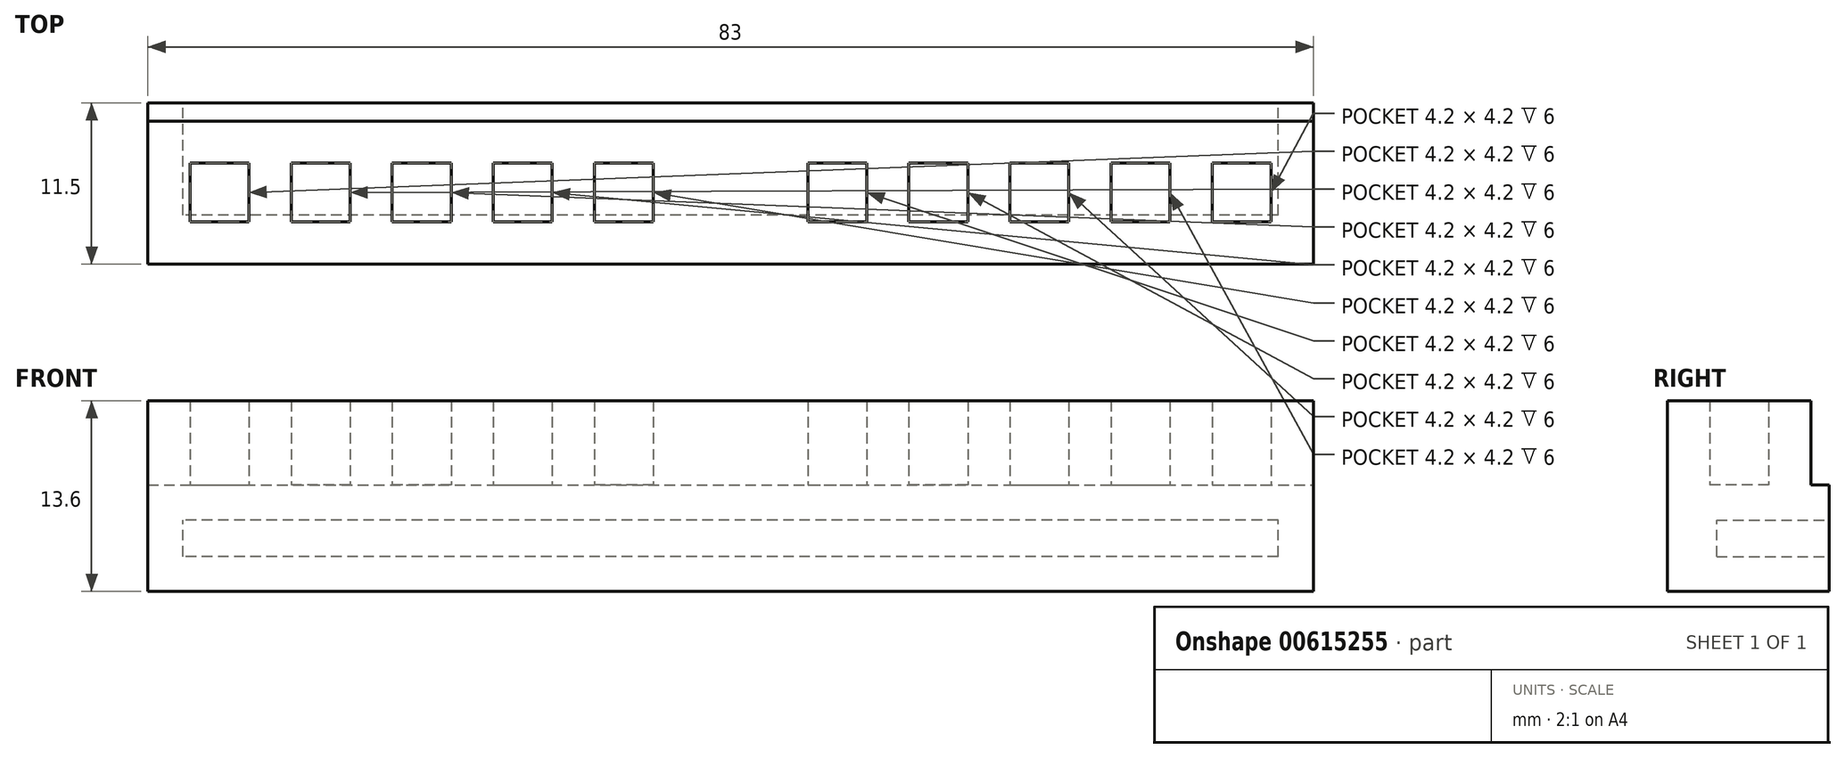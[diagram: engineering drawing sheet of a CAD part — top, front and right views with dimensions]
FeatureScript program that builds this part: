
annotation { "Feature Type Name" : "Feature", "Feature Type Description" : "" }
export const myFeature = defineFeature(function(context is Context, id is Id, definition is map)
    precondition{}
    {
        {
            var Q0;
            Q0=qCreatedBy(makeId("Front.planeOp"),FACE);
            var sketch = newSketch(context, id + "F0", { "sketchPlane" : qUnion([Q0])});
            skLineSegment(sketch, "E0.bottom", {"start": v(41.5, -3.8) * mm, "end": v(-41.5, -3.8) * mm});
            skLineSegment(sketch, "E0.top", {"start": v(41.5, 3.8) * mm, "end": v(-41.5, 3.8) * mm});
            skLineSegment(sketch, "E0.left", {"start": v(41.5, -3.8) * mm, "end": v(41.5, 3.8) * mm});
            skLineSegment(sketch, "E0.right", {"start": v(-41.5, -3.8) * mm, "end": v(-41.5, 3.8) * mm});
            skPoint(sketch, "E0.middle", {"position": v(0, 0) * mm});
            skLineSegment(sketch, "E1.bottom", {"start": v(39, -1.3) * mm, "end": v(-39, -1.3) * mm});
            skLineSegment(sketch, "E1.top", {"start": v(39, 1.3) * mm, "end": v(-39, 1.3) * mm});
            skLineSegment(sketch, "E1.left", {"start": v(39, -1.3) * mm, "end": v(39, 1.3) * mm});
            skLineSegment(sketch, "E1.right", {"start": v(-39, -1.3) * mm, "end": v(-39, 1.3) * mm});
            skSolve(sketch);
        }
        {
            var Q0;
            Q0=makeQuery(id+"F0.imprint","IMPRINT",FACE,{"disambiguationData":[TD([[makeQuery(id+"F0.imprint","IMPRINT",EDGE,{"derivedFrom":sQuery(id+"F0.wireOp",EDGE,"E0.bottom")}),-1.0]])]});
            extrude(context, id + "F1", {"entities" : qUnion([Q0]), "depth" : 8 * mm, "offsetDistance" : 25 * mm});
        }
        {
            var Q0;
            Q0=makeQuery(id+"F1.opExtrude","CAP_FACE",FACE,{"disambiguationData":[OSD([sQuery(id+"F0.wireOp",EDGE,"E0.bottom"),sQuery(id+"F0.wireOp",EDGE,"E0.top"),sQuery(id+"F0.wireOp",EDGE,"E0.left"),sQuery(id+"F0.wireOp",EDGE,"E0.right"),sQuery(id+"F0.wireOp",EDGE,"E1.bottom"),sQuery(id+"F0.wireOp",EDGE,"E1.top"),sQuery(id+"F0.wireOp",EDGE,"E1.left"),sQuery(id+"F0.wireOp",EDGE,"E1.right")])],"isStart":false});
            var sketch = newSketch(context, id + "F2", { "sketchPlane" : qUnion([Q0])});
            skLineSegment(sketch, "E2.bottom", {"start": v(-41.5, 3.8) * mm, "end": v(41.5, 3.8) * mm});
            skLineSegment(sketch, "E2.top", {"start": v(-41.5, -3.8) * mm, "end": v(41.5, -3.8) * mm});
            skLineSegment(sketch, "E2.left", {"start": v(-41.5, 3.8) * mm, "end": v(-41.5, -3.8) * mm});
            skLineSegment(sketch, "E2.right", {"start": v(41.5, 3.8) * mm, "end": v(41.5, -3.8) * mm});
            skSolve(sketch);
        }
        {
            var Q0;
            Q0=makeQuery(id+"F2.imprint","IMPRINT",FACE,{"disambiguationData":[TD([[makeQuery(id+"F2.imprint","IMPRINT",EDGE,{"derivedFrom":sQuery(id+"F2.wireOp",EDGE,"E2.bottom")}),1.0]])]});
            var Q1;
            Q1=makeQuery(id+"F2.imprint","IMPRINT",FACE,{"disambiguationData":[TD([[makeQuery(id+"F2.imprint","IMPRINT",EDGE,{"derivedFrom":makeQuery(id+"F1.opExtrude","CAP_EDGE",EDGE,{"disambiguationData":[OSD([sQuery(id+"F0.wireOp",EDGE,"E1.bottom")])],"isStart":false})}),-1.0]])]});
            extrude(context, id + "F3", {"entities" : qUnion([Q0, Q1]), "operationType" : NewBodyOperationType.ADD, "depth" : 3.5 * mm, "offsetDistance" : 25 * mm});
        }
        {
            var Q0;
            Q0=makeQuery(id+"F3.boolean.opBoolean","MERGE",FACE,{"derivedFrom":[makeQuery(id+"F1.opExtrude","SWEPT_FACE",FACE,{"disambiguationData":[OSD([sQuery(id+"F0.wireOp",EDGE,"E0.top")])]}),makeQuery(id+"F3.opExtrude","SWEPT_FACE",FACE,{"disambiguationData":[OSD([sQuery(id+"F2.wireOp",EDGE,"E2.bottom")])]})]});
            var sketch = newSketch(context, id + "F4", { "sketchPlane" : qUnion([Q0])});
            skLineSegment(sketch, "E3.bottom", {"start": v(-41.5, -11.5) * mm, "end": v(41.5, -11.5) * mm});
            skLineSegment(sketch, "E3.top", {"start": v(-41.5, -1.3) * mm, "end": v(41.5, -1.3) * mm});
            skLineSegment(sketch, "E3.left", {"start": v(-41.5, -11.5) * mm, "end": v(-41.5, -1.3) * mm});
            skLineSegment(sketch, "E3.right", {"start": v(41.5, -11.5) * mm, "end": v(41.5, -1.3) * mm});
            skLineSegment(sketch, "E4", {"start": v(-5.5, -1.3) * mm, "end": v(-5.5, -11.5) * mm});
            skLineSegment(sketch, "E5", {"start": v(-9.7, -1.3) * mm, "end": v(-9.7, -11.5) * mm});
            skLineSegment(sketch, "E6", {"start": v(-12.7, -1.3) * mm, "end": v(-12.7, -11.5) * mm});
            skLineSegment(sketch, "E7", {"start": v(-16.9, -1.3) * mm, "end": v(-16.9, -11.5) * mm});
            skLineSegment(sketch, "E8", {"start": v(-19.9, -1.3) * mm, "end": v(-19.9, -11.5) * mm});
            skLineSegment(sketch, "E9", {"start": v(-24.1, -1.3) * mm, "end": v(-24.1, -11.5) * mm});
            skLineSegment(sketch, "E10", {"start": v(-27.1, -1.3) * mm, "end": v(-27.1, -11.5) * mm});
            skLineSegment(sketch, "E11", {"start": v(-31.3, -1.3) * mm, "end": v(-31.3, -11.5) * mm});
            skLineSegment(sketch, "E12", {"start": v(-34.3, -1.3) * mm, "end": v(-34.3, -11.5) * mm});
            skLineSegment(sketch, "E13", {"start": v(-38.5, -1.3) * mm, "end": v(-38.5, -11.5) * mm});
            skLineSegment(sketch, "E14", {"start": v(0, 0) * mm, "end": v(0, -13.13) * mm, "construction": true});
            skLineSegment(sketch, "E15.MirrorCS", {"start": v(38.5, -1.3) * mm, "end": v(38.5, -11.5) * mm});
            skLineSegment(sketch, "E16.MirrorCS", {"start": v(19.9, -1.3) * mm, "end": v(19.9, -11.5) * mm});
            skLineSegment(sketch, "E17.MirrorCS", {"start": v(24.1, -1.3) * mm, "end": v(24.1, -11.5) * mm});
            skLineSegment(sketch, "E18.MirrorCS", {"start": v(34.3, -1.3) * mm, "end": v(34.3, -11.5) * mm});
            skLineSegment(sketch, "E19.MirrorCS", {"start": v(27.1, -1.3) * mm, "end": v(27.1, -11.5) * mm});
            skLineSegment(sketch, "E20.MirrorCS", {"start": v(16.9, -1.3) * mm, "end": v(16.9, -11.5) * mm});
            skLineSegment(sketch, "E21.MirrorCS", {"start": v(9.7, -1.3) * mm, "end": v(9.7, -11.5) * mm});
            skLineSegment(sketch, "E22.MirrorCS", {"start": v(12.7, -1.3) * mm, "end": v(12.7, -11.5) * mm});
            skLineSegment(sketch, "E23.MirrorCS", {"start": v(31.3, -1.3) * mm, "end": v(31.3, -11.5) * mm});
            skLineSegment(sketch, "E24.MirrorCS", {"start": v(5.5, -1.3) * mm, "end": v(5.5, -11.5) * mm});
            skLineSegment(sketch, "E25", {"start": v(-41.5, -4.3) * mm, "end": v(41.5, -4.3) * mm});
            skLineSegment(sketch, "E26", {"start": v(41.5, -8.5) * mm, "end": v(-41.5, -8.5) * mm});
            skSolve(sketch);
        }
        {
            var Q0;
            {var subQ1=sQuery(id+"F4.wireOp",EDGE,"E3.top");var subQ3=sQuery(id+"F4.wireOp",EDGE,"E13");var subQ4=makeQuery(id+"F4.imprint","INTERSECT",VERTEX,{"derivedFrom":[subQ1,subQ3]});Q0=makeQuery(id+"F4.imprint","IMPRINT",FACE,{"disambiguationData":[TD([[makeQuery(id+"F4.imprint","IMPRINT",EDGE,{"disambiguationData":[TD([[subQ4,-1.0]])],"derivedFrom":subQ3}),-1.0]])]});}
            var Q1;
            {var subQ0=sQuery(id+"F4.wireOp",EDGE,"E25");var subQ1=sQuery(id+"F4.wireOp",EDGE,"E3.left");var subQ2=makeQuery(id+"F4.imprint","INTERSECT",VERTEX,{"derivedFrom":[subQ1,subQ0]});Q1=makeQuery(id+"F4.imprint","IMPRINT",FACE,{"disambiguationData":[TD([[makeQuery(id+"F4.imprint","IMPRINT",EDGE,{"disambiguationData":[TD([[subQ2,1.0]])],"derivedFrom":subQ1}),-1.0]])]});}
            var Q2;
            {var subQ0=sQuery(id+"F4.wireOp",EDGE,"E12");var subQ1=sQuery(id+"F4.wireOp",EDGE,"E3.top");var subQ2=makeQuery(id+"F4.imprint","INTERSECT",VERTEX,{"derivedFrom":[subQ1,subQ0]});Q2=makeQuery(id+"F4.imprint","IMPRINT",FACE,{"disambiguationData":[TD([[makeQuery(id+"F4.imprint","IMPRINT",EDGE,{"disambiguationData":[TD([[subQ2,1.0]])],"derivedFrom":subQ1}),-1.0]])]});}
            var Q3;
            {var subQ0=sQuery(id+"F4.wireOp",EDGE,"E3.left");var subQ1=sQuery(id+"F4.wireOp",EDGE,"E3.bottom");var subQ2=makeQuery(id+"F4.imprint","INTERSECT",VERTEX,{"derivedFrom":[subQ1,subQ0]});Q3=makeQuery(id+"F4.imprint","IMPRINT",FACE,{"disambiguationData":[TD([[makeQuery(id+"F4.imprint","IMPRINT",EDGE,{"disambiguationData":[TD([[subQ2,1.0]])],"derivedFrom":subQ1}),-1.0]])]});}
            var Q4;
            {var subQ0=sQuery(id+"F4.wireOp",EDGE,"E12");var subQ1=sQuery(id+"F4.wireOp",EDGE,"E3.bottom");var subQ2=makeQuery(id+"F4.imprint","INTERSECT",VERTEX,{"derivedFrom":[subQ1,subQ0]});Q4=makeQuery(id+"F4.imprint","IMPRINT",FACE,{"disambiguationData":[TD([[makeQuery(id+"F4.imprint","IMPRINT",EDGE,{"disambiguationData":[TD([[subQ2,-1.0]])],"derivedFrom":subQ1}),-1.0]])]});}
            var Q5;
            {var subQ0=sQuery(id+"F4.wireOp",EDGE,"E11");var subQ1=sQuery(id+"F4.wireOp",EDGE,"E3.bottom");var subQ2=makeQuery(id+"F4.imprint","INTERSECT",VERTEX,{"derivedFrom":[subQ1,subQ0]});Q5=makeQuery(id+"F4.imprint","IMPRINT",FACE,{"disambiguationData":[TD([[makeQuery(id+"F4.imprint","IMPRINT",EDGE,{"disambiguationData":[TD([[subQ2,-1.0]])],"derivedFrom":subQ1}),-1.0]])]});}
            var Q6;
            {var subQ0=sQuery(id+"F4.wireOp",EDGE,"E25");var subQ1=sQuery(id+"F4.wireOp",EDGE,"E11");var subQ2=makeQuery(id+"F4.imprint","INTERSECT",VERTEX,{"derivedFrom":[subQ1,subQ0]});Q6=makeQuery(id+"F4.imprint","IMPRINT",FACE,{"disambiguationData":[TD([[makeQuery(id+"F4.imprint","IMPRINT",EDGE,{"disambiguationData":[TD([[subQ2,-1.0]])],"derivedFrom":subQ1}),-1.0]])]});}
            var Q7;
            {var subQ0=sQuery(id+"F4.wireOp",EDGE,"E11");var subQ1=sQuery(id+"F4.wireOp",EDGE,"E3.top");var subQ2=makeQuery(id+"F4.imprint","INTERSECT",VERTEX,{"derivedFrom":[subQ1,subQ0]});Q7=makeQuery(id+"F4.imprint","IMPRINT",FACE,{"disambiguationData":[TD([[makeQuery(id+"F4.imprint","IMPRINT",EDGE,{"disambiguationData":[TD([[subQ2,1.0]])],"derivedFrom":subQ1}),-1.0]])]});}
            var Q8;
            {var subQ0=sQuery(id+"F4.wireOp",EDGE,"E10");var subQ1=sQuery(id+"F4.wireOp",EDGE,"E3.top");var subQ2=makeQuery(id+"F4.imprint","INTERSECT",VERTEX,{"derivedFrom":[subQ1,subQ0]});Q8=makeQuery(id+"F4.imprint","IMPRINT",FACE,{"disambiguationData":[TD([[makeQuery(id+"F4.imprint","IMPRINT",EDGE,{"disambiguationData":[TD([[subQ2,1.0]])],"derivedFrom":subQ1}),-1.0]])]});}
            var Q9;
            {var subQ0=sQuery(id+"F4.wireOp",EDGE,"E10");var subQ1=sQuery(id+"F4.wireOp",EDGE,"E3.bottom");var subQ2=makeQuery(id+"F4.imprint","INTERSECT",VERTEX,{"derivedFrom":[subQ1,subQ0]});Q9=makeQuery(id+"F4.imprint","IMPRINT",FACE,{"disambiguationData":[TD([[makeQuery(id+"F4.imprint","IMPRINT",EDGE,{"disambiguationData":[TD([[subQ2,-1.0]])],"derivedFrom":subQ1}),-1.0]])]});}
            var Q10;
            {var subQ0=sQuery(id+"F4.wireOp",EDGE,"E9");var subQ1=sQuery(id+"F4.wireOp",EDGE,"E3.bottom");var subQ2=makeQuery(id+"F4.imprint","INTERSECT",VERTEX,{"derivedFrom":[subQ1,subQ0]});Q10=makeQuery(id+"F4.imprint","IMPRINT",FACE,{"disambiguationData":[TD([[makeQuery(id+"F4.imprint","IMPRINT",EDGE,{"disambiguationData":[TD([[subQ2,-1.0]])],"derivedFrom":subQ1}),-1.0]])]});}
            var Q11;
            {var subQ0=sQuery(id+"F4.wireOp",EDGE,"E8");var subQ1=sQuery(id+"F4.wireOp",EDGE,"E3.bottom");var subQ2=makeQuery(id+"F4.imprint","INTERSECT",VERTEX,{"derivedFrom":[subQ1,subQ0]});Q11=makeQuery(id+"F4.imprint","IMPRINT",FACE,{"disambiguationData":[TD([[makeQuery(id+"F4.imprint","IMPRINT",EDGE,{"disambiguationData":[TD([[subQ2,-1.0]])],"derivedFrom":subQ1}),-1.0]])]});}
            var Q12;
            {var subQ0=sQuery(id+"F4.wireOp",EDGE,"E8");var subQ1=sQuery(id+"F4.wireOp",EDGE,"E3.top");var subQ2=makeQuery(id+"F4.imprint","INTERSECT",VERTEX,{"derivedFrom":[subQ1,subQ0]});Q12=makeQuery(id+"F4.imprint","IMPRINT",FACE,{"disambiguationData":[TD([[makeQuery(id+"F4.imprint","IMPRINT",EDGE,{"disambiguationData":[TD([[subQ2,1.0]])],"derivedFrom":subQ1}),-1.0]])]});}
            var Q13;
            {var subQ0=sQuery(id+"F4.wireOp",EDGE,"E9");var subQ1=sQuery(id+"F4.wireOp",EDGE,"E3.top");var subQ2=makeQuery(id+"F4.imprint","INTERSECT",VERTEX,{"derivedFrom":[subQ1,subQ0]});Q13=makeQuery(id+"F4.imprint","IMPRINT",FACE,{"disambiguationData":[TD([[makeQuery(id+"F4.imprint","IMPRINT",EDGE,{"disambiguationData":[TD([[subQ2,1.0]])],"derivedFrom":subQ1}),-1.0]])]});}
            var Q14;
            {var subQ0=sQuery(id+"F4.wireOp",EDGE,"E25");var subQ1=sQuery(id+"F4.wireOp",EDGE,"E9");var subQ2=makeQuery(id+"F4.imprint","INTERSECT",VERTEX,{"derivedFrom":[subQ1,subQ0]});Q14=makeQuery(id+"F4.imprint","IMPRINT",FACE,{"disambiguationData":[TD([[makeQuery(id+"F4.imprint","IMPRINT",EDGE,{"disambiguationData":[TD([[subQ2,-1.0]])],"derivedFrom":subQ1}),-1.0]])]});}
            var Q15;
            {var subQ0=sQuery(id+"F4.wireOp",EDGE,"E7");var subQ1=sQuery(id+"F4.wireOp",EDGE,"E3.top");var subQ2=makeQuery(id+"F4.imprint","INTERSECT",VERTEX,{"derivedFrom":[subQ1,subQ0]});Q15=makeQuery(id+"F4.imprint","IMPRINT",FACE,{"disambiguationData":[TD([[makeQuery(id+"F4.imprint","IMPRINT",EDGE,{"disambiguationData":[TD([[subQ2,1.0]])],"derivedFrom":subQ1}),-1.0]])]});}
            var Q16;
            {var subQ0=sQuery(id+"F4.wireOp",EDGE,"E25");var subQ1=sQuery(id+"F4.wireOp",EDGE,"E7");var subQ2=makeQuery(id+"F4.imprint","INTERSECT",VERTEX,{"derivedFrom":[subQ1,subQ0]});Q16=makeQuery(id+"F4.imprint","IMPRINT",FACE,{"disambiguationData":[TD([[makeQuery(id+"F4.imprint","IMPRINT",EDGE,{"disambiguationData":[TD([[subQ2,-1.0]])],"derivedFrom":subQ1}),-1.0]])]});}
            var Q17;
            {var subQ0=sQuery(id+"F4.wireOp",EDGE,"E7");var subQ1=sQuery(id+"F4.wireOp",EDGE,"E3.bottom");var subQ2=makeQuery(id+"F4.imprint","INTERSECT",VERTEX,{"derivedFrom":[subQ1,subQ0]});Q17=makeQuery(id+"F4.imprint","IMPRINT",FACE,{"disambiguationData":[TD([[makeQuery(id+"F4.imprint","IMPRINT",EDGE,{"disambiguationData":[TD([[subQ2,-1.0]])],"derivedFrom":subQ1}),-1.0]])]});}
            var Q18;
            {var subQ0=sQuery(id+"F4.wireOp",EDGE,"E6");var subQ1=sQuery(id+"F4.wireOp",EDGE,"E3.bottom");var subQ2=makeQuery(id+"F4.imprint","INTERSECT",VERTEX,{"derivedFrom":[subQ1,subQ0]});Q18=makeQuery(id+"F4.imprint","IMPRINT",FACE,{"disambiguationData":[TD([[makeQuery(id+"F4.imprint","IMPRINT",EDGE,{"disambiguationData":[TD([[subQ2,-1.0]])],"derivedFrom":subQ1}),-1.0]])]});}
            var Q19;
            {var subQ0=sQuery(id+"F4.wireOp",EDGE,"E5");var subQ1=sQuery(id+"F4.wireOp",EDGE,"E3.bottom");var subQ2=makeQuery(id+"F4.imprint","INTERSECT",VERTEX,{"derivedFrom":[subQ1,subQ0]});Q19=makeQuery(id+"F4.imprint","IMPRINT",FACE,{"disambiguationData":[TD([[makeQuery(id+"F4.imprint","IMPRINT",EDGE,{"disambiguationData":[TD([[subQ2,-1.0]])],"derivedFrom":subQ1}),-1.0]])]});}
            var Q20;
            {var subQ0=sQuery(id+"F4.wireOp",EDGE,"E25");var subQ1=sQuery(id+"F4.wireOp",EDGE,"E5");var subQ2=makeQuery(id+"F4.imprint","INTERSECT",VERTEX,{"derivedFrom":[subQ1,subQ0]});Q20=makeQuery(id+"F4.imprint","IMPRINT",FACE,{"disambiguationData":[TD([[makeQuery(id+"F4.imprint","IMPRINT",EDGE,{"disambiguationData":[TD([[subQ2,-1.0]])],"derivedFrom":subQ1}),-1.0]])]});}
            var Q21;
            {var subQ0=sQuery(id+"F4.wireOp",EDGE,"E6");var subQ1=sQuery(id+"F4.wireOp",EDGE,"E3.top");var subQ2=makeQuery(id+"F4.imprint","INTERSECT",VERTEX,{"derivedFrom":[subQ1,subQ0]});Q21=makeQuery(id+"F4.imprint","IMPRINT",FACE,{"disambiguationData":[TD([[makeQuery(id+"F4.imprint","IMPRINT",EDGE,{"disambiguationData":[TD([[subQ2,1.0]])],"derivedFrom":subQ1}),-1.0]])]});}
            var Q22;
            {var subQ0=sQuery(id+"F4.wireOp",EDGE,"E5");var subQ1=sQuery(id+"F4.wireOp",EDGE,"E3.top");var subQ2=makeQuery(id+"F4.imprint","INTERSECT",VERTEX,{"derivedFrom":[subQ1,subQ0]});Q22=makeQuery(id+"F4.imprint","IMPRINT",FACE,{"disambiguationData":[TD([[makeQuery(id+"F4.imprint","IMPRINT",EDGE,{"disambiguationData":[TD([[subQ2,1.0]])],"derivedFrom":subQ1}),-1.0]])]});}
            var Q23;
            {var subQ0=sQuery(id+"F4.wireOp",EDGE,"E4");var subQ1=sQuery(id+"F4.wireOp",EDGE,"E3.top");var subQ2=makeQuery(id+"F4.imprint","INTERSECT",VERTEX,{"derivedFrom":[subQ1,subQ0]});Q23=makeQuery(id+"F4.imprint","IMPRINT",FACE,{"disambiguationData":[TD([[makeQuery(id+"F4.imprint","IMPRINT",EDGE,{"disambiguationData":[TD([[subQ2,1.0]])],"derivedFrom":subQ1}),-1.0]])]});}
            var Q24;
            {var subQ0=sQuery(id+"F4.wireOp",EDGE,"E4");var subQ1=sQuery(id+"F4.wireOp",EDGE,"E3.top");var subQ2=makeQuery(id+"F4.imprint","INTERSECT",VERTEX,{"derivedFrom":[subQ1,subQ0]});Q24=makeQuery(id+"F4.imprint","IMPRINT",FACE,{"disambiguationData":[TD([[makeQuery(id+"F4.imprint","IMPRINT",EDGE,{"disambiguationData":[TD([[subQ2,-1.0]])],"derivedFrom":subQ1}),-1.0]])]});}
            var Q25;
            {var subQ0=sQuery(id+"F4.wireOp",EDGE,"E25");var subQ1=sQuery(id+"F4.wireOp",EDGE,"E4");var subQ2=makeQuery(id+"F4.imprint","INTERSECT",VERTEX,{"derivedFrom":[subQ1,subQ0]});Q25=makeQuery(id+"F4.imprint","IMPRINT",FACE,{"disambiguationData":[TD([[makeQuery(id+"F4.imprint","IMPRINT",EDGE,{"disambiguationData":[TD([[subQ2,-1.0]])],"derivedFrom":subQ1}),1.0]])]});}
            var Q26;
            {var subQ0=sQuery(id+"F4.wireOp",EDGE,"E4");var subQ1=sQuery(id+"F4.wireOp",EDGE,"E3.bottom");var subQ2=makeQuery(id+"F4.imprint","INTERSECT",VERTEX,{"derivedFrom":[subQ1,subQ0]});Q26=makeQuery(id+"F4.imprint","IMPRINT",FACE,{"disambiguationData":[TD([[makeQuery(id+"F4.imprint","IMPRINT",EDGE,{"disambiguationData":[TD([[subQ2,-1.0]])],"derivedFrom":subQ1}),-1.0]])]});}
            var Q27;
            {var subQ0=sQuery(id+"F4.wireOp",EDGE,"E4");var subQ1=sQuery(id+"F4.wireOp",EDGE,"E3.bottom");var subQ2=makeQuery(id+"F4.imprint","INTERSECT",VERTEX,{"derivedFrom":[subQ1,subQ0]});Q27=makeQuery(id+"F4.imprint","IMPRINT",FACE,{"disambiguationData":[TD([[makeQuery(id+"F4.imprint","IMPRINT",EDGE,{"disambiguationData":[TD([[subQ2,1.0]])],"derivedFrom":subQ1}),-1.0]])]});}
            var Q28;
            {var subQ0=sQuery(id+"F4.wireOp",EDGE,"E21.MirrorCS");var subQ1=sQuery(id+"F4.wireOp",EDGE,"E3.top");var subQ2=makeQuery(id+"F4.imprint","INTERSECT",VERTEX,{"derivedFrom":[subQ1,subQ0]});Q28=makeQuery(id+"F4.imprint","IMPRINT",FACE,{"disambiguationData":[TD([[makeQuery(id+"F4.imprint","IMPRINT",EDGE,{"disambiguationData":[TD([[subQ2,1.0]])],"derivedFrom":subQ1}),-1.0]])]});}
            var Q29;
            {var subQ0=sQuery(id+"F4.wireOp",EDGE,"E21.MirrorCS");var subQ1=sQuery(id+"F4.wireOp",EDGE,"E3.bottom");var subQ2=makeQuery(id+"F4.imprint","INTERSECT",VERTEX,{"derivedFrom":[subQ1,subQ0]});Q29=makeQuery(id+"F4.imprint","IMPRINT",FACE,{"disambiguationData":[TD([[makeQuery(id+"F4.imprint","IMPRINT",EDGE,{"disambiguationData":[TD([[subQ2,-1.0]])],"derivedFrom":subQ1}),-1.0]])]});}
            var Q30;
            {var subQ0=sQuery(id+"F4.wireOp",EDGE,"E21.MirrorCS");var subQ1=sQuery(id+"F4.wireOp",EDGE,"E3.bottom");var subQ2=makeQuery(id+"F4.imprint","INTERSECT",VERTEX,{"derivedFrom":[subQ1,subQ0]});Q30=makeQuery(id+"F4.imprint","IMPRINT",FACE,{"disambiguationData":[TD([[makeQuery(id+"F4.imprint","IMPRINT",EDGE,{"disambiguationData":[TD([[subQ2,1.0]])],"derivedFrom":subQ1}),-1.0]])]});}
            var Q31;
            {var subQ0=sQuery(id+"F4.wireOp",EDGE,"E21.MirrorCS");var subQ1=sQuery(id+"F4.wireOp",EDGE,"E3.top");var subQ2=makeQuery(id+"F4.imprint","INTERSECT",VERTEX,{"derivedFrom":[subQ1,subQ0]});Q31=makeQuery(id+"F4.imprint","IMPRINT",FACE,{"disambiguationData":[TD([[makeQuery(id+"F4.imprint","IMPRINT",EDGE,{"disambiguationData":[TD([[subQ2,-1.0]])],"derivedFrom":subQ1}),-1.0]])]});}
            var Q32;
            {var subQ0=sQuery(id+"F4.wireOp",EDGE,"E20.MirrorCS");var subQ1=sQuery(id+"F4.wireOp",EDGE,"E3.top");var subQ2=makeQuery(id+"F4.imprint","INTERSECT",VERTEX,{"derivedFrom":[subQ1,subQ0]});Q32=makeQuery(id+"F4.imprint","IMPRINT",FACE,{"disambiguationData":[TD([[makeQuery(id+"F4.imprint","IMPRINT",EDGE,{"disambiguationData":[TD([[subQ2,1.0]])],"derivedFrom":subQ1}),-1.0]])]});}
            var Q33;
            {var subQ0=sQuery(id+"F4.wireOp",EDGE,"E25");var subQ1=sQuery(id+"F4.wireOp",EDGE,"E21.MirrorCS");var subQ2=makeQuery(id+"F4.imprint","INTERSECT",VERTEX,{"derivedFrom":[subQ1,subQ0]});Q33=makeQuery(id+"F4.imprint","IMPRINT",FACE,{"disambiguationData":[TD([[makeQuery(id+"F4.imprint","IMPRINT",EDGE,{"disambiguationData":[TD([[subQ2,-1.0]])],"derivedFrom":subQ1}),1.0]])]});}
            var Q34;
            {var subQ0=sQuery(id+"F4.wireOp",EDGE,"E16.MirrorCS");var subQ1=sQuery(id+"F4.wireOp",EDGE,"E3.top");var subQ2=makeQuery(id+"F4.imprint","INTERSECT",VERTEX,{"derivedFrom":[subQ1,subQ0]});Q34=makeQuery(id+"F4.imprint","IMPRINT",FACE,{"disambiguationData":[TD([[makeQuery(id+"F4.imprint","IMPRINT",EDGE,{"disambiguationData":[TD([[subQ2,1.0]])],"derivedFrom":subQ1}),-1.0]])]});}
            var Q35;
            {var subQ0=sQuery(id+"F4.wireOp",EDGE,"E16.MirrorCS");var subQ1=sQuery(id+"F4.wireOp",EDGE,"E3.top");var subQ2=makeQuery(id+"F4.imprint","INTERSECT",VERTEX,{"derivedFrom":[subQ1,subQ0]});Q35=makeQuery(id+"F4.imprint","IMPRINT",FACE,{"disambiguationData":[TD([[makeQuery(id+"F4.imprint","IMPRINT",EDGE,{"disambiguationData":[TD([[subQ2,-1.0]])],"derivedFrom":subQ1}),-1.0]])]});}
            var Q36;
            {var subQ0=sQuery(id+"F4.wireOp",EDGE,"E17.MirrorCS");var subQ1=sQuery(id+"F4.wireOp",EDGE,"E3.top");var subQ2=makeQuery(id+"F4.imprint","INTERSECT",VERTEX,{"derivedFrom":[subQ1,subQ0]});Q36=makeQuery(id+"F4.imprint","IMPRINT",FACE,{"disambiguationData":[TD([[makeQuery(id+"F4.imprint","IMPRINT",EDGE,{"disambiguationData":[TD([[subQ2,-1.0]])],"derivedFrom":subQ1}),-1.0]])]});}
            var Q37;
            {var subQ0=sQuery(id+"F4.wireOp",EDGE,"E19.MirrorCS");var subQ1=sQuery(id+"F4.wireOp",EDGE,"E3.top");var subQ2=makeQuery(id+"F4.imprint","INTERSECT",VERTEX,{"derivedFrom":[subQ1,subQ0]});Q37=makeQuery(id+"F4.imprint","IMPRINT",FACE,{"disambiguationData":[TD([[makeQuery(id+"F4.imprint","IMPRINT",EDGE,{"disambiguationData":[TD([[subQ2,-1.0]])],"derivedFrom":subQ1}),-1.0]])]});}
            var Q38;
            {var subQ0=sQuery(id+"F4.wireOp",EDGE,"E18.MirrorCS");var subQ1=sQuery(id+"F4.wireOp",EDGE,"E3.top");var subQ2=makeQuery(id+"F4.imprint","INTERSECT",VERTEX,{"derivedFrom":[subQ1,subQ0]});Q38=makeQuery(id+"F4.imprint","IMPRINT",FACE,{"disambiguationData":[TD([[makeQuery(id+"F4.imprint","IMPRINT",EDGE,{"disambiguationData":[TD([[subQ2,1.0]])],"derivedFrom":subQ1}),-1.0]])]});}
            var Q39;
            {var subQ0=sQuery(id+"F4.wireOp",EDGE,"E15.MirrorCS");var subQ1=sQuery(id+"F4.wireOp",EDGE,"E3.top");var subQ2=makeQuery(id+"F4.imprint","INTERSECT",VERTEX,{"derivedFrom":[subQ1,subQ0]});Q39=makeQuery(id+"F4.imprint","IMPRINT",FACE,{"disambiguationData":[TD([[makeQuery(id+"F4.imprint","IMPRINT",EDGE,{"disambiguationData":[TD([[subQ2,1.0]])],"derivedFrom":subQ1}),-1.0]])]});}
            var Q40;
            {var subQ1=sQuery(id+"F4.wireOp",EDGE,"E3.top");var subQ3=sQuery(id+"F4.wireOp",EDGE,"E15.MirrorCS");var subQ4=makeQuery(id+"F4.imprint","INTERSECT",VERTEX,{"derivedFrom":[subQ1,subQ3]});Q40=makeQuery(id+"F4.imprint","IMPRINT",FACE,{"disambiguationData":[TD([[makeQuery(id+"F4.imprint","IMPRINT",EDGE,{"disambiguationData":[TD([[subQ4,-1.0]])],"derivedFrom":subQ3}),1.0]])]});}
            var Q41;
            {var subQ0=sQuery(id+"F4.wireOp",EDGE,"E25");var subQ1=sQuery(id+"F4.wireOp",EDGE,"E3.right");var subQ2=makeQuery(id+"F4.imprint","INTERSECT",VERTEX,{"derivedFrom":[subQ1,subQ0]});Q41=makeQuery(id+"F4.imprint","IMPRINT",FACE,{"disambiguationData":[TD([[makeQuery(id+"F4.imprint","IMPRINT",EDGE,{"disambiguationData":[TD([[subQ2,1.0]])],"derivedFrom":subQ1}),1.0]])]});}
            var Q42;
            {var subQ0=sQuery(id+"F4.wireOp",EDGE,"E3.right");var subQ1=sQuery(id+"F4.wireOp",EDGE,"E3.bottom");var subQ2=makeQuery(id+"F4.imprint","INTERSECT",VERTEX,{"derivedFrom":[subQ1,subQ0]});Q42=makeQuery(id+"F4.imprint","IMPRINT",FACE,{"disambiguationData":[TD([[makeQuery(id+"F4.imprint","IMPRINT",EDGE,{"disambiguationData":[TD([[subQ2,-1.0]])],"derivedFrom":subQ1}),-1.0]])]});}
            var Q43;
            {var subQ0=sQuery(id+"F4.wireOp",EDGE,"E15.MirrorCS");var subQ1=sQuery(id+"F4.wireOp",EDGE,"E3.bottom");var subQ2=makeQuery(id+"F4.imprint","INTERSECT",VERTEX,{"derivedFrom":[subQ1,subQ0]});Q43=makeQuery(id+"F4.imprint","IMPRINT",FACE,{"disambiguationData":[TD([[makeQuery(id+"F4.imprint","IMPRINT",EDGE,{"disambiguationData":[TD([[subQ2,-1.0]])],"derivedFrom":subQ1}),-1.0]])]});}
            var Q44;
            {var subQ0=sQuery(id+"F4.wireOp",EDGE,"E18.MirrorCS");var subQ1=sQuery(id+"F4.wireOp",EDGE,"E3.bottom");var subQ2=makeQuery(id+"F4.imprint","INTERSECT",VERTEX,{"derivedFrom":[subQ1,subQ0]});Q44=makeQuery(id+"F4.imprint","IMPRINT",FACE,{"disambiguationData":[TD([[makeQuery(id+"F4.imprint","IMPRINT",EDGE,{"disambiguationData":[TD([[subQ2,-1.0]])],"derivedFrom":subQ1}),-1.0]])]});}
            var Q45;
            {var subQ0=sQuery(id+"F4.wireOp",EDGE,"E19.MirrorCS");var subQ1=sQuery(id+"F4.wireOp",EDGE,"E3.bottom");var subQ2=makeQuery(id+"F4.imprint","INTERSECT",VERTEX,{"derivedFrom":[subQ1,subQ0]});Q45=makeQuery(id+"F4.imprint","IMPRINT",FACE,{"disambiguationData":[TD([[makeQuery(id+"F4.imprint","IMPRINT",EDGE,{"disambiguationData":[TD([[subQ2,1.0]])],"derivedFrom":subQ1}),-1.0]])]});}
            var Q46;
            {var subQ0=sQuery(id+"F4.wireOp",EDGE,"E17.MirrorCS");var subQ1=sQuery(id+"F4.wireOp",EDGE,"E3.bottom");var subQ2=makeQuery(id+"F4.imprint","INTERSECT",VERTEX,{"derivedFrom":[subQ1,subQ0]});Q46=makeQuery(id+"F4.imprint","IMPRINT",FACE,{"disambiguationData":[TD([[makeQuery(id+"F4.imprint","IMPRINT",EDGE,{"disambiguationData":[TD([[subQ2,1.0]])],"derivedFrom":subQ1}),-1.0]])]});}
            var Q47;
            {var subQ0=sQuery(id+"F4.wireOp",EDGE,"E16.MirrorCS");var subQ1=sQuery(id+"F4.wireOp",EDGE,"E3.bottom");var subQ2=makeQuery(id+"F4.imprint","INTERSECT",VERTEX,{"derivedFrom":[subQ1,subQ0]});Q47=makeQuery(id+"F4.imprint","IMPRINT",FACE,{"disambiguationData":[TD([[makeQuery(id+"F4.imprint","IMPRINT",EDGE,{"disambiguationData":[TD([[subQ2,1.0]])],"derivedFrom":subQ1}),-1.0]])]});}
            var Q48;
            {var subQ0=sQuery(id+"F4.wireOp",EDGE,"E16.MirrorCS");var subQ1=sQuery(id+"F4.wireOp",EDGE,"E3.bottom");var subQ2=makeQuery(id+"F4.imprint","INTERSECT",VERTEX,{"derivedFrom":[subQ1,subQ0]});Q48=makeQuery(id+"F4.imprint","IMPRINT",FACE,{"disambiguationData":[TD([[makeQuery(id+"F4.imprint","IMPRINT",EDGE,{"disambiguationData":[TD([[subQ2,-1.0]])],"derivedFrom":subQ1}),-1.0]])]});}
            var Q49;
            {var subQ0=sQuery(id+"F4.wireOp",EDGE,"E20.MirrorCS");var subQ1=sQuery(id+"F4.wireOp",EDGE,"E3.bottom");var subQ2=makeQuery(id+"F4.imprint","INTERSECT",VERTEX,{"derivedFrom":[subQ1,subQ0]});Q49=makeQuery(id+"F4.imprint","IMPRINT",FACE,{"disambiguationData":[TD([[makeQuery(id+"F4.imprint","IMPRINT",EDGE,{"disambiguationData":[TD([[subQ2,-1.0]])],"derivedFrom":subQ1}),-1.0]])]});}
            var Q50;
            {var subQ0=sQuery(id+"F4.wireOp",EDGE,"E25");var subQ1=sQuery(id+"F4.wireOp",EDGE,"E16.MirrorCS");var subQ2=makeQuery(id+"F4.imprint","INTERSECT",VERTEX,{"derivedFrom":[subQ1,subQ0]});Q50=makeQuery(id+"F4.imprint","IMPRINT",FACE,{"disambiguationData":[TD([[makeQuery(id+"F4.imprint","IMPRINT",EDGE,{"disambiguationData":[TD([[subQ2,-1.0]])],"derivedFrom":subQ1}),-1.0]])]});}
            var Q51;
            {var subQ0=sQuery(id+"F4.wireOp",EDGE,"E25");var subQ1=sQuery(id+"F4.wireOp",EDGE,"E17.MirrorCS");var subQ2=makeQuery(id+"F4.imprint","INTERSECT",VERTEX,{"derivedFrom":[subQ1,subQ0]});Q51=makeQuery(id+"F4.imprint","IMPRINT",FACE,{"disambiguationData":[TD([[makeQuery(id+"F4.imprint","IMPRINT",EDGE,{"disambiguationData":[TD([[subQ2,-1.0]])],"derivedFrom":subQ1}),1.0]])]});}
            var Q52;
            {var subQ0=sQuery(id+"F4.wireOp",EDGE,"E25");var subQ1=sQuery(id+"F4.wireOp",EDGE,"E18.MirrorCS");var subQ2=makeQuery(id+"F4.imprint","INTERSECT",VERTEX,{"derivedFrom":[subQ1,subQ0]});Q52=makeQuery(id+"F4.imprint","IMPRINT",FACE,{"disambiguationData":[TD([[makeQuery(id+"F4.imprint","IMPRINT",EDGE,{"disambiguationData":[TD([[subQ2,-1.0]])],"derivedFrom":subQ1}),-1.0]])]});}
            extrude(context, id + "F5", {"entities" : qUnion([Q0, Q1, Q2, Q3, Q4, Q5, Q6, Q7, Q8, Q9, Q10, Q11, Q12, Q13, Q14, Q15, Q16, Q17, Q18, Q19, Q20, Q21, Q22, Q23, Q24, Q25, Q26, Q27, Q28, Q29, Q30, Q31, Q32, Q33, Q34, Q35, Q36, Q37, Q38, Q39, Q40, Q41, Q42, Q43, Q44, Q45, Q46, Q47, Q48, Q49, Q50, Q51, Q52]), "operationType" : NewBodyOperationType.ADD, "depth" : 6 * mm, "offsetDistance" : 25 * mm});
        }
    });
